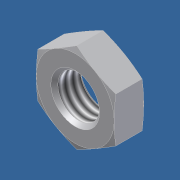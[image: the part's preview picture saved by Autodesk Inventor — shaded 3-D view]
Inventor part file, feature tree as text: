
AUTODESK INVENTOR PART (.ipt)
format: ipt  version: 2012 (Build 160160000, 160)  size: 129,024 bytes
history: native  units: in
note: dims shown in document units (in); Inventor stores cm internally (conversion verified against a paired STEP export)
features: other x70, sketch x3, revolve x2, extrude x1, thread x1
ambient origin geometry x8: Origin, YZ Plane, XZ Plane, XY Plane, X Axis, Y Axis, Z Axis, Center Point
bodies: Solid1 (feature_tree)
feature tree (77):
  sketch  "Sketch_8"  dims[d0=360.0deg d1=0.19in d2=0.0in]
  sketch  "Sketch_10"  dims[d3=360.0deg d4=0.19in d5=0.0in]
  revolve  "Revolution1"  [1 undecoded]
  extrude  "Extrusion1"  Depth=0.19in TaperAngle=0.0deg
  revolve  "Revolution2"  [1 undecoded]
  thread  "Thread1"  [1 undecoded]
  other  "NUT_XY"
  other  "NUT_YZ"
  other  "NUT_ZX"
  other  "NUT_X"
  other  "NUT_Y"
  other  "NUT_Z"
  other  "NUT_Center"
  other  "a1_XY"
  other  "a1_YZ"
  other  "a1_ZX"
  other  "a1_X"
  other  "a1_Y"
  other  "a1_Z"
  other  "a1_Center"
  other  "a2_XY"
  other  "a2_YZ"
  other  "a2_ZX"
  other  "a2_X"
  other  "a2_Y"
  other  "a2_Z"
  other  "a2_Center"
  other  "b1_XY"
  other  "b1_YZ"
  other  "b1_ZX"
  other  "b1_X"
  other  "b1_Y"
  other  "b1_Z"
  other  "b1_Center"
  other  "b2_XY"
  other  "b2_YZ"
  other  "b2_ZX"
  other  "b2_X"
  other  "b2_Y"
  other  "b2_Z"
  other  "b2_Center"
  other  "e_XY"
  other  "e_YZ"
  other  "e_ZX"
  other  "e_X"
  other  "e_Y"
  other  "e_Z"
  other  "e_Center"
  other  "th1_XY"
  other  "th1_YZ"
  other  "th1_ZX"
  other  "th1_X"
  other  "th1_Y"
  other  "th1_Z"
  other  "th1_Center"
  other  "th2_XY"
  other  "th2_YZ"
  other  "th2_ZX"
  other  "th2_X"
  other  "th2_Y"
  other  "th2_Z"
  other  "th2_Center"
  other  "ol1_XY"
  other  "ol1_YZ"
  other  "ol1_ZX"
  other  "ol1_X"
  other  "ol1_Y"
  other  "ol1_Z"
  other  "ol1_Center"
  other  "ol2_XY"
  other  "ol2_YZ"
  other  "ol2_ZX"
  other  "ol2_X"
  other  "ol2_Y"
  other  "ol2_Z"
  other  "ol2_Center"
  sketch  "Sketch_11"
note: 3 required parameter values undecoded (feature->parameter linkage not recoverable at this tier; creation-order binding heuristic only, values carry confidence <= 0.55)